# Revit family: COD3M 6 (6RED+4RJ45)
name_source: partatom
category: Aparatos eléctricos
revit_build: Autodesk Revit 2016 (Build: 20150220_1215(x64)
units: mm (PartAtom-declared; Revit-internal decimal feet)

## family parameters
Anfitrión = Cara
Compartido = No
Corte con vacíos al cargar = No
Cota de conector redondo = Diámetro de uso
Mantener orientación de anotación = No
Número OmniClass = 23.80.50.11.11
Punto de cálculo de habitación = No
Tipo de pieza = Normal
Título OmniClass = Receptacle Terminal Units

## types (3) — shared parameters
COD3M (AltoxLargoxAncho) = 3000 x 147,5 x 112 mm
Capacidad = Ilimitados
Carga eléctrica = Potencia
Compatibilidad = Gama 45
Composición = Perfil de aluminio en dos caras a 3m, Tapa da aluminio de 3m (2ud), Guía de aluminio de anclaje a techo de 1,5m, Embellecedor superior, Tornillería de suelo (4ud), Zócalo
Código de montaje = D5020100
Descripción = Torre de conexiones CODM 45
Elevación por defecto = 1200 mm
Fabricante = MMCONECTA
Factor de potencia = 1
Instalación = De suelo a techo
Modelo = CODM45 - COD3M
Normativas = UNE 60670 / Marcado CE
Polos = 1
Potencia aparente = 3500 W
URL = http://www.mmconecta.com
Voltaje = 230 V
Ø tubos G = 25 mm  [stored 0.082021 ft]

## per-type parameters (varying)
| type | Acabado | Materia prima |
| Módulo /4 - Blanco | Blanco nieve RAL9019 | Policarbonato libre de halógenos |
| Módulo /6 - Grafito | Grafito RAL7021 | Policarbonato libre de halógenos |
| Módulo /9 - Aluminio | Aluminio anodizado | Aluminio anodizado |

note: [stored X ft] marks values corroborated as IEEE doubles in the binary element streams (Revit-internal decimal feet)
